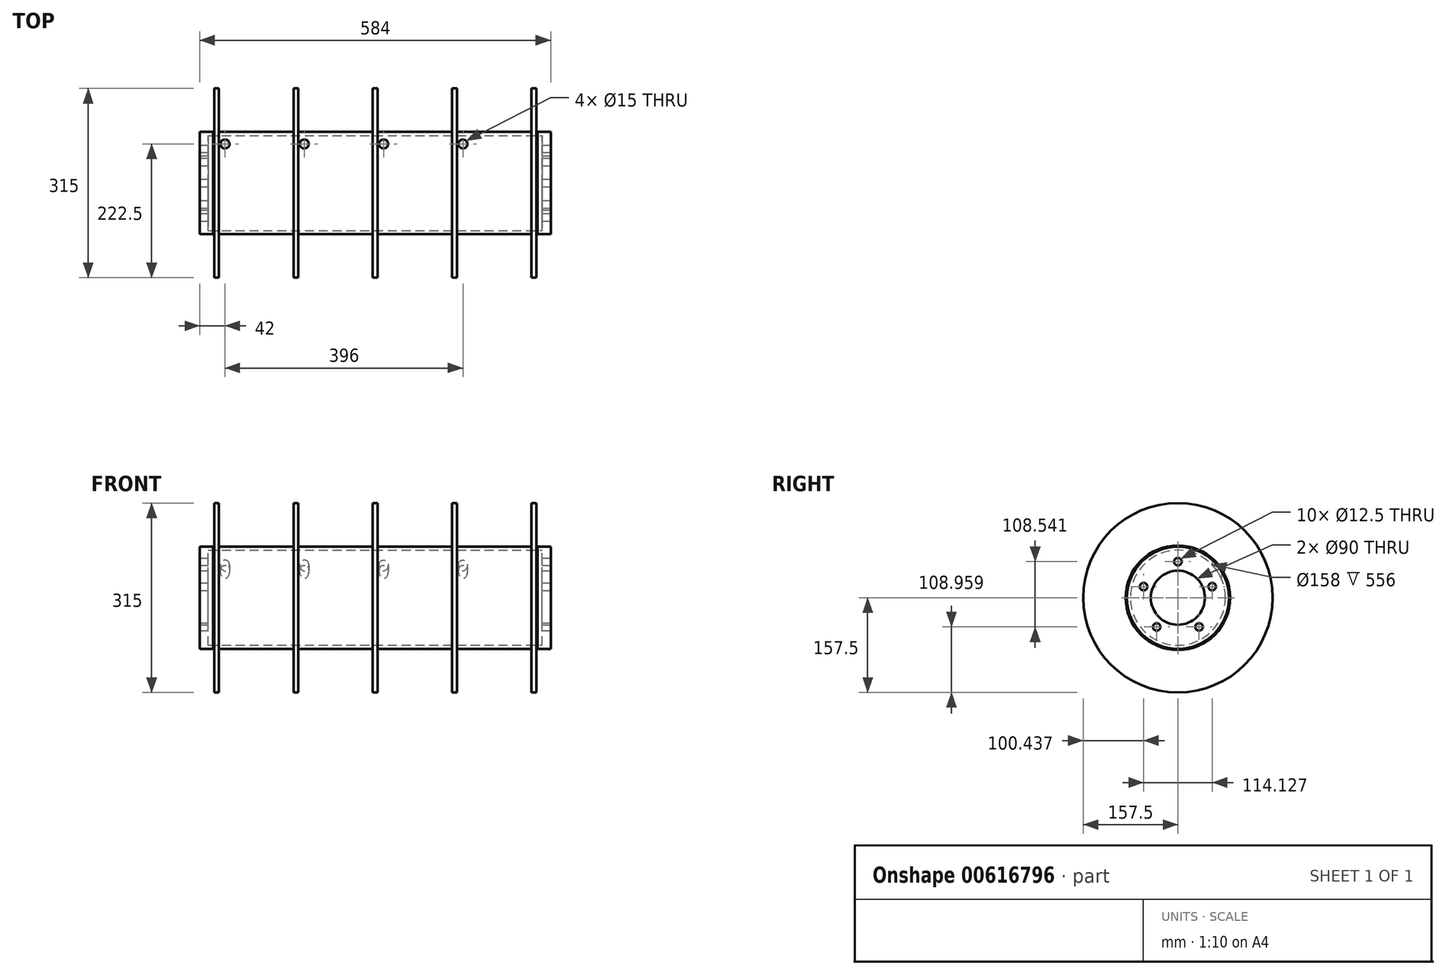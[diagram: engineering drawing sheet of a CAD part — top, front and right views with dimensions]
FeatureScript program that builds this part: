
annotation { "Feature Type Name" : "Feature", "Feature Type Description" : "" }
export const myFeature = defineFeature(function(context is Context, id is Id, definition is map)
    precondition{}
    {
        {
            var Q0;
            Q0=qCreatedBy(makeId("Front.planeOp"),FACE);
            var sketch = newSketch(context, id + "F0", { "sketchPlane" : qUnion([Q0])});
            skLineSegment(sketch, "E0", {"start": v(0, 157.5) * mm, "end": v(-4, 157.5) * mm});
            skLineSegment(sketch, "E1", {"start": v(-4, 157.5) * mm, "end": v(-4, 85) * mm});
            skLineSegment(sketch, "E2", {"start": v(-4, 85) * mm, "end": v(-128, 85) * mm});
            skLineSegment(sketch, "E3", {"start": v(-128, 85) * mm, "end": v(-128, 157.5) * mm});
            skLineSegment(sketch, "E4", {"start": v(-128, 157.5) * mm, "end": v(-136, 157.5) * mm});
            skLineSegment(sketch, "E5", {"start": v(-136, 157.5) * mm, "end": v(-136, 85) * mm});
            skLineSegment(sketch, "E6", {"start": v(-136, 85) * mm, "end": v(-260, 85) * mm});
            skLineSegment(sketch, "E7", {"start": v(-260, 85) * mm, "end": v(-260, 157.5) * mm});
            skLineSegment(sketch, "E8", {"start": v(-260, 157.5) * mm, "end": v(-268, 157.5) * mm});
            skLineSegment(sketch, "E9", {"start": v(-268, 157.5) * mm, "end": v(-268, 87) * mm});
            skLineSegment(sketch, "E10", {"start": v(-268, 87) * mm, "end": v(-270, 87) * mm});
            skLineSegment(sketch, "E11", {"start": v(-270, 87) * mm, "end": v(-270, 85) * mm});
            skLineSegment(sketch, "E12", {"start": v(-270, 85) * mm, "end": v(-292, 85) * mm});
            skLineSegment(sketch, "E13", {"start": v(-292, 85) * mm, "end": v(-292, 45) * mm});
            skLineSegment(sketch, "E14", {"start": v(-292, 45) * mm, "end": v(-278, 45) * mm});
            skLineSegment(sketch, "E15", {"start": v(-278, 45) * mm, "end": v(-278, 79) * mm});
            skLineSegment(sketch, "E16", {"start": v(-278, 79) * mm, "end": v(0, 79) * mm});
            skLineSegment(sketch, "E17", {"start": v(0, 0) * mm, "end": v(-323.34, 0) * mm, "construction": true});
            skLineSegment(sketch, "E18.MirrorCS", {"start": v(268, 87) * mm, "end": v(270, 87) * mm});
            skLineSegment(sketch, "E19.MirrorCS", {"start": v(270, 85) * mm, "end": v(292, 85) * mm});
            skLineSegment(sketch, "E20.MirrorCS", {"start": v(270, 87) * mm, "end": v(270, 85) * mm});
            skLineSegment(sketch, "E21.MirrorCS", {"start": v(128, 157.5) * mm, "end": v(136, 157.5) * mm});
            skLineSegment(sketch, "E22.MirrorCS", {"start": v(0, 157.5) * mm, "end": v(4, 157.5) * mm});
            skLineSegment(sketch, "E23.MirrorCS", {"start": v(260, 157.5) * mm, "end": v(268, 157.5) * mm});
            skLineSegment(sketch, "E24.MirrorCS", {"start": v(292, 45) * mm, "end": v(278, 45) * mm});
            skLineSegment(sketch, "E25.MirrorCS", {"start": v(136, 85) * mm, "end": v(260, 85) * mm});
            skLineSegment(sketch, "E26.MirrorCS", {"start": v(136, 157.5) * mm, "end": v(136, 85) * mm});
            skLineSegment(sketch, "E27.MirrorCS", {"start": v(278, 79) * mm, "end": v(0, 79) * mm});
            skLineSegment(sketch, "E28.MirrorCS", {"start": v(128, 85) * mm, "end": v(128, 157.5) * mm});
            skLineSegment(sketch, "E29.MirrorCS", {"start": v(4, 85) * mm, "end": v(128, 85) * mm});
            skLineSegment(sketch, "E30.MirrorCS", {"start": v(4, 157.5) * mm, "end": v(4, 85) * mm});
            skLineSegment(sketch, "E31.MirrorCS", {"start": v(268, 157.5) * mm, "end": v(268, 87) * mm});
            skLineSegment(sketch, "E32.MirrorCS", {"start": v(260, 85) * mm, "end": v(260, 157.5) * mm});
            skLineSegment(sketch, "E33.MirrorCS", {"start": v(278, 45) * mm, "end": v(278, 79) * mm});
            skLineSegment(sketch, "E34.MirrorCS", {"start": v(292, 85) * mm, "end": v(292, 45) * mm});
            skSolve(sketch);
        }
        {
            var Q0;
            Q0 = qSketchRegion(id + "F0", true);
            var Q1;
            Q1=sQuery(id+"F0.wireOp",EDGE,"E17");
            revolve(context, id + "F1", {"surfaceOperationType" : NewSurfaceOperationType.NEW, "entities" : qUnion([Q0]), "axis" : qUnion([Q1]), "revolveType" : RevolveType.FULL});
        }
        {
            var Q0;
            Q0=makeQuery(id+"F1.opRevolve","SWEPT_FACE",FACE,{"disambiguationData":[OSD([sQuery(id+"F0.wireOp",EDGE,"E34.MirrorCS")])]});
            var sketch = newSketch(context, id + "F2", { "sketchPlane" : qUnion([Q0])});
            skCircle(sketch, "E35", {"center": v(0, 0) * mm, "radius": 60 * mm, "construction": true});
            skCircle(sketch, "E36", {"center": v(0, 60) * mm, "radius": 6.25 * mm});
            skCircle(sketch, "E37.1.0", {"center": v(-57.06, 18.54) * mm, "radius": 6.25 * mm});
            skCircle(sketch, "E37.2.0", {"center": v(-35.27, -48.54) * mm, "radius": 6.25 * mm});
            skCircle(sketch, "E37.3.0", {"center": v(35.27, -48.54) * mm, "radius": 6.25 * mm});
            skCircle(sketch, "E37.4.0", {"center": v(57.06, 18.54) * mm, "radius": 6.25 * mm});
            skSolve(sketch);
        }
        {
            var Q0;
            Q0 = qSketchRegion(id + "F2", true);
            extrude(context, id + "F3", {"entities" : qUnion([Q0]), "operationType" : NewBodyOperationType.REMOVE, "endBound" : BoundingType.THROUGH_ALL, "oppositeDirection" : true, "depth" : 25 * mm, "offsetDistance" : 25 * mm});
        }
        {
            var Q0;
            Q0=qCreatedBy(makeId("Top.planeOp"),FACE);
            var sketch = newSketch(context, id + "F4", { "sketchPlane" : qUnion([Q0])});
            skCircle(sketch, "E38", {"center": v(-250, 65) * mm, "radius": 7.5 * mm});
            skLineSegment(sketch, "E39", {"start": v(-260, 85) * mm, "end": v(-136, 85) * mm, "construction": true});
            skCircle(sketch, "E40.1.0.0", {"center": v(-118, 65) * mm, "radius": 7.5 * mm});
            skCircle(sketch, "E40.2.0.0", {"center": v(14, 65) * mm, "radius": 7.5 * mm});
            skCircle(sketch, "E40.3.0.0", {"center": v(146, 65) * mm, "radius": 7.5 * mm});
            skLineSegment(sketch, "E40.direction1", {"start": v(-250, 65) * mm, "end": v(-118, 65) * mm, "construction": true});
            skSolve(sketch);
        }
        {
            var Q0;
            Q0 = qSketchRegion(id + "F4", true);
            extrude(context, id + "F5", {"entities" : qUnion([Q0]), "operationType" : NewBodyOperationType.REMOVE, "depth" : 116 * mm, "offsetDistance" : 25 * mm});
        }
    });
